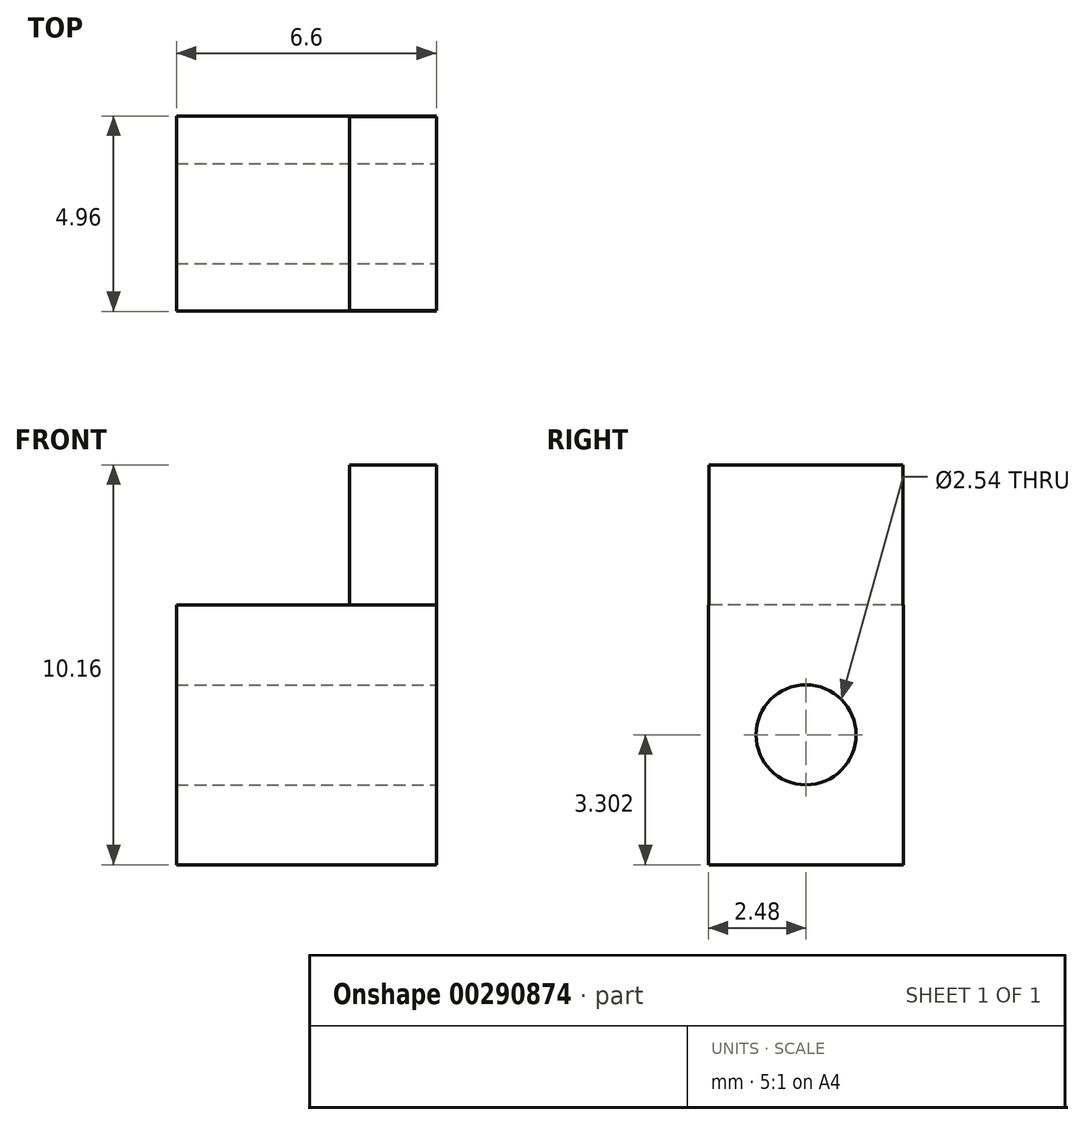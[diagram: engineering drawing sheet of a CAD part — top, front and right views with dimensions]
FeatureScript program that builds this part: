
annotation { "Feature Type Name" : "Feature", "Feature Type Description" : "" }
export const myFeature = defineFeature(function(context is Context, id is Id, definition is map)
    precondition{}
    {
        {
            var Q0;
            Q0=qCreatedBy(makeId("Top.planeOp"),FACE);
            var sketch = newSketch(context, id + "F0", { "sketchPlane" : qUnion([Q0])});
            skLineSegment(sketch, "E0.bottom", {"start": v(3.3, 2.48) * mm, "end": v(-3.3, 2.48) * mm});
            skLineSegment(sketch, "E0.top", {"start": v(3.3, -2.48) * mm, "end": v(-3.3, -2.48) * mm});
            skLineSegment(sketch, "E0.left", {"start": v(3.3, 2.48) * mm, "end": v(3.3, -2.48) * mm});
            skLineSegment(sketch, "E0.right", {"start": v(-3.3, 2.48) * mm, "end": v(-3.3, -2.48) * mm});
            skPoint(sketch, "E0.middle", {"position": v(0, 0) * mm});
            skSolve(sketch);
        }
        {
            var Q0;
            Q0 = qSketchRegion(id + "F0", true);
            extrude(context, id + "F1", {"entities" : qUnion([Q0]), "depth" : 6.6 * mm});
        }
        {
            var Q0;
            Q0=qCreatedBy(makeId("Top.planeOp"),FACE);
            var sketch = newSketch(context, id + "F2", { "sketchPlane" : qUnion([Q0])});
            skLineSegment(sketch, "E1", {"start": v(0, 0) * mm, "end": v(3.3, 0) * mm, "construction": true});
            skLineSegment(sketch, "E2", {"start": v(0, 0) * mm, "end": v(-3.3, 0) * mm, "construction": true});
            skLineSegment(sketch, "E3", {"start": v(3.3, 0) * mm, "end": v(1.1, 0) * mm, "construction": true});
            skLineSegment(sketch, "E4.bottom", {"start": v(1.1, 0) * mm, "end": v(3.3, 0) * mm});
            skLineSegment(sketch, "E4.top", {"start": v(1.1, 2.46) * mm, "end": v(3.3, 2.46) * mm});
            skLineSegment(sketch, "E4.left", {"start": v(1.1, 0) * mm, "end": v(1.1, 2.46) * mm});
            skLineSegment(sketch, "E4.right", {"start": v(3.3, 0) * mm, "end": v(3.3, 2.46) * mm});
            skLineSegment(sketch, "E5.MirrorCS", {"start": v(3.3, 0) * mm, "end": v(3.3, -2.46) * mm});
            skLineSegment(sketch, "E6.MirrorCS", {"start": v(1.1, -2.46) * mm, "end": v(3.3, -2.46) * mm});
            skLineSegment(sketch, "E7.MirrorCS", {"start": v(1.1, 0) * mm, "end": v(1.1, -2.46) * mm});
            skSolve(sketch);
        }
        {
            var Q0;
            Q0 = qSketchRegion(id + "F2", true);
            extrude(context, id + "F3", {"entities" : qUnion([Q0]), "operationType" : NewBodyOperationType.ADD, "depth" : 10.16 * mm});
        }
        {
            var Q0;
            Q0=qCreatedBy(makeId("Right.planeOp"),FACE);
            var sketch = newSketch(context, id + "F4", { "sketchPlane" : qUnion([Q0])});
            skLineSegment(sketch, "E8", {"start": v(0, 0) * mm, "end": v(0, 6.6) * mm, "construction": true});
            skLineSegment(sketch, "E9", {"start": v(0, 0) * mm, "end": v(0, 3.3) * mm, "construction": true});
            skCircle(sketch, "E10", {"center": v(0, 3.3) * mm, "radius": 1.27 * mm});
            skSolve(sketch);
        }
        {
            var Q0;
            Q0 = qSketchRegion(id + "F4", true);
            extrude(context, id + "F5", {"entities" : qUnion([Q0]), "operationType" : NewBodyOperationType.REMOVE, "oppositeDirection" : true, "depth" : 3.3 * mm});
        }
        {
            var Q0;
            Q0 = qSketchRegion(id + "F4", true);
            extrude(context, id + "F6", {"entities" : qUnion([Q0]), "operationType" : NewBodyOperationType.REMOVE, "depth" : 3.3 * mm});
        }
    });
